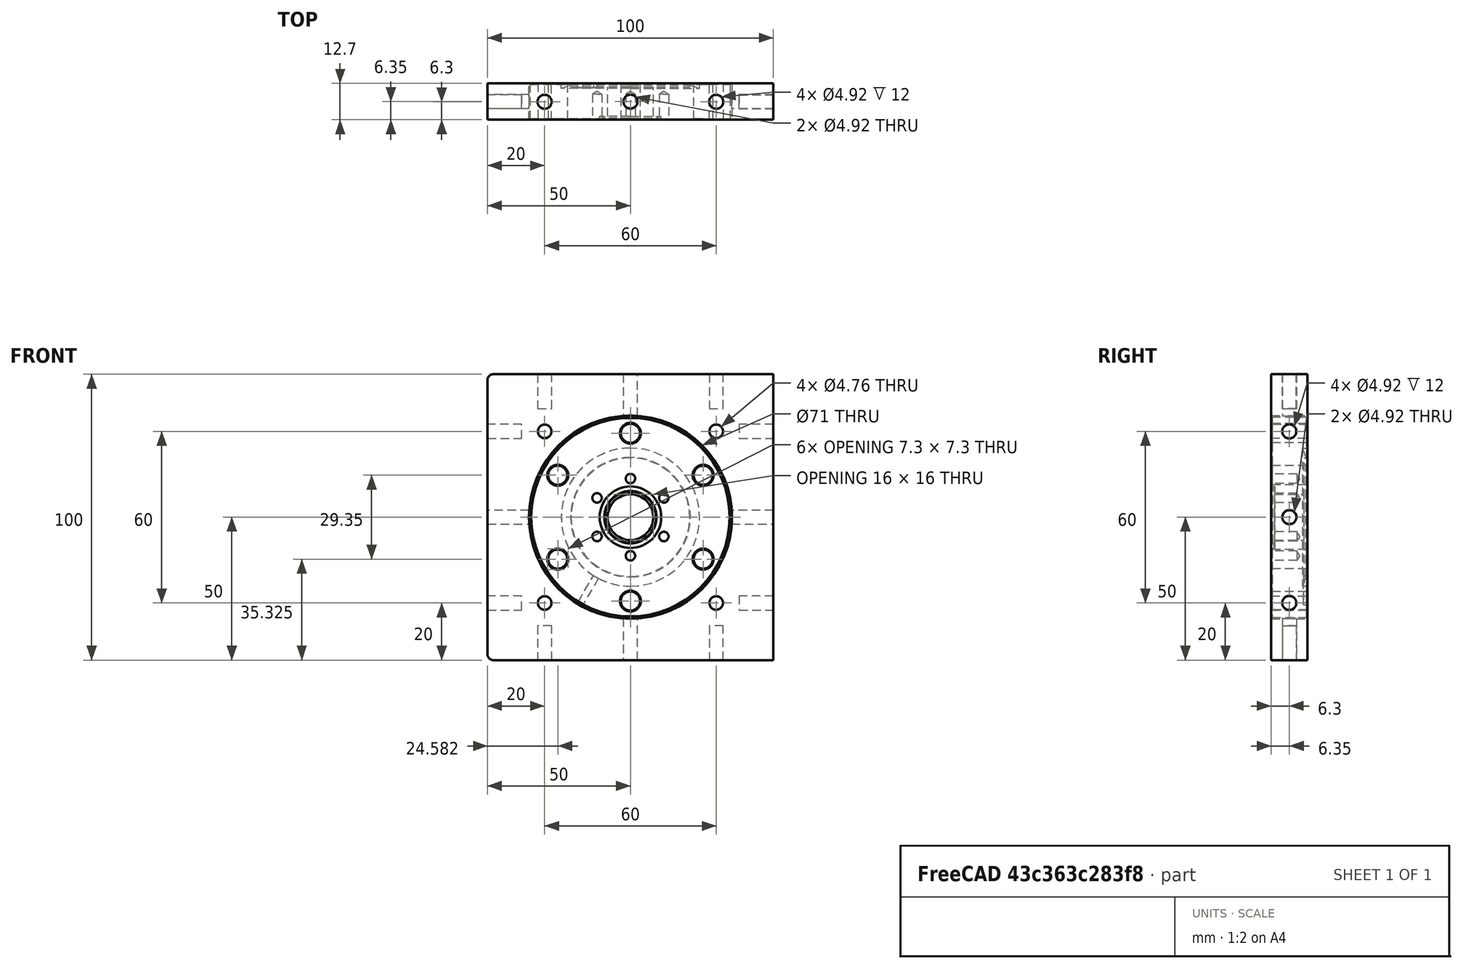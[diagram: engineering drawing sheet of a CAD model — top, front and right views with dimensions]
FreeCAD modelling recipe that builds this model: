
FCSTD DOCUMENT  (FreeCAD 0.20R29603 (Git))
Label: MechanicalCF35Mount001
License: All rights reserved
LicenseURL: http://en.wikipedia.org/wiki/All_rights_reserved
objects: Part::Feature×20, Part::Cylinder×15, TechDraw::DrawViewDimension×13, Part::Compound×12, TechDraw::DrawProjGroupItem×5, Part::Cut×4, Part::Box×1, Part::Fillet×1, TechDraw::DrawSVGTemplate×1, TechDraw::DrawProjGroup×1, TechDraw::DrawPage×1
note: 53 computed .brp shape members not serialized (recipe doc carries the construction recipe); baked Part::Feature solids carry a one-line shape summary decoded from their .brp

FEATURE [Part::Feature] Solid  label="Hositrad_CFA35-16D"
  shape: bbox 70 x 12.7 x 70 mm, 88 faces (baked)
FEATURE [Part::Feature] _7192_01_CF
  shape: bbox 33.78 x 40.23 x 14.22 mm, 39 faces, 0 solids (baked)
FEATURE [Part::Feature] _7192_01_CF001
  Placement = pos=(0,0,-39.0113) rot=(1,0,0;1.5708rad)
  shape: bbox 14 x 7.506 x 26.34 mm, 46 faces, 0 solids (baked)
FEATURE [Part::Feature] _7192_01_CF002
  Placement = pos=(0,0,-58.2625) rot=(-0.03621,0.706643,0.706643;3.21398rad)
  shape: bbox 18.12 x 10.39 x 7.838 mm, 29 faces, 0 solids (baked)
FEATURE [Part::Feature] _7192_01_CF003
  Placement = pos=(0,0,-42.2965) rot=(0.8891,-0.323652,-0.323652;1.68807rad)
  shape: bbox 16.99 x 16.03 x 5.603 mm, 25 faces, 0 solids (baked)
FEATURE [Part::Feature] _7192_01_CF004
  Placement = pos=(0,0,-35.56) rot=(0,0.707107,-0.707107;3.14159rad)
  shape: bbox 22.78 x 12.72 x 33.85 mm, 35 faces, 0 solids (baked)
FEATURE [Part::Feature] _7192_01_CF005
  Placement = pos=(0,0,-36.7339) rot=(0.997746,-0.047454,-0.047454;1.57305rad)
  shape: bbox 7.007 x 7.007 x 0.8128 mm, 6 faces, 0 solids (baked)
FEATURE [Part::Feature] _7192_01_CF006
  Placement = pos=(0,0,-66.0654) rot=(0.57735,0.57735,0.57735;2.0944rad)
  shape: bbox 2.416 x 2.416 x 39.37 mm, 29 faces, 0 solids (baked)
FEATURE [Part::Feature] _7192_01_CF007
  Placement = pos=(0,0,-32.2253) rot=(0.196732,0.693288,-0.693288;3.5301rad)
  shape: bbox 26.96 x 26.96 x 13.28 mm, 55 faces, 0 solids (baked)
FEATURE [Part::Feature] _7192_01_CF008
  Placement = pos=(0,0,-46.1699) rot=(0.196732,0.693288,-0.693288;3.5301rad)
  shape: bbox 34.28 x 29.27 x 4.775 mm, 16 faces, 0 solids (baked)
FEATURE [Part::Feature] _7192_01_CF009
  Placement = pos=(0,0,-22.86) rot=(0.196732,0.693288,-0.693288;3.5301rad)
  shape: bbox 24.3 x 24.3 x 12.6 mm, 19 faces, 0 solids (baked)
FEATURE [Part::Feature] _7192_01_CF010
  Placement = pos=(0,0,-12.7) rot=(0.196732,0.693288,-0.693288;3.5301rad)
  shape: bbox 26.42 x 26.42 x 12.7 mm, 14 faces, 0 solids (baked)
FEATURE [Part::Feature] _7192_01_CF011
  Placement = pos=(0,0,-42.1821) rot=(0.196732,0.693288,-0.693288;3.5301rad)
  shape: bbox 43.95 x 37.52 x 5.044 mm, 27 faces, 0 solids (baked)
FEATURE [Part::Feature] _7192_01_CF012
  Placement = pos=(0,0,-35.56) rot=(0.079728,0.704856,0.704856;2.98247rad)
  shape: bbox 15.4 x 15.4 x 39.12 mm, 6 faces, 0 solids (baked)
FEATURE [Part::Feature] _7192_01_CF013
  Placement = pos=(0,0,-26.6954) rot=(0.165786,0.697322,0.697322;2.81301rad)
  shape: bbox 5.339 x 4.281 x 34.06 mm, 6 faces, 0 solids (baked)
FEATURE [Part::Feature] _7192_01_CF014
  Placement = pos=(0,0,6.7564) rot=(0.205998,0.691941,-0.691941;3.54791rad)
  shape: bbox 9.907 x 7.446 x 1.311 mm, 4 faces, 0 solids (baked)
FEATURE [Part::Feature] _7192_01_CF015
  Placement = pos=(0,0,-7.9756) rot=(1,0,0;1.5708rad)
  shape: bbox 22.78 x 12.72 x 22.32 mm, 35 faces, 0 solids (baked)
FEATURE [Part::Feature] _7192_01_CF016
  Placement = pos=(0,0,22.3805) rot=(0.205998,0.691941,-0.691941;3.54791rad)
  shape: bbox 3.344 x 3.344 x 15.27 mm, 29 faces, 0 solids (baked)
FEATURE [Part::Feature] _7192_01_CF017
  Placement = pos=(0,0,6.7564) rot=(1,0,0;1.5708rad)
  shape: bbox 10.8 x 10.8 x 1.524 mm, 10 faces, 0 solids (baked)
FEATURE [Part::Compound] Compound  label="CF16BNCFeedthrough"
  Links = -> [_7192_01_CF,_7192_01_CF001,_7192_01_CF002,_7192_01_CF003,_7192_01_CF004,_7192_01_CF005,_7192_01_CF006,_7192_01_CF007,_7192_01_CF008,_7192_01_CF009,_7192_01_CF010,_7192_01_CF011,_7192_01_CF012,_7192_01_CF013,_7192_01_CF014,_7192_01_CF015,_7192_01_CF016,_7192_01_CF017]
  Placement = pos=(0,0,0) rot=(-1,0,0;1.5708rad)
FEATURE [Part::Box] Box  label="Würfel"
  AttacherType = Attacher::AttachEngine3D
  Height = 100
  Length = 100
  Placement = pos=(-50,0,-50) rot=(0,0,1;0rad)
  Width = 12.7
FEATURE [Part::Cylinder] Cylinder  label="Zylinder"
  Angle = 360
  AttacherType = Attacher::AttachEngine3D
  FirstAngle = 0
  Height = 12.7
  Placement = pos=(0,12.7,0) rot=(1,0,0;1.5708rad)
  Radius = 35.5
  SecondAngle = 0
FEATURE [Part::Cut] Cut
  Base = -> Box
  Tool = -> Cylinder
FEATURE [Part::Cylinder] Cylinder001  label="Zylinder001"
  Angle = 360
  AttacherType = Attacher::AttachEngine3D
  FirstAngle = 0
  Height = 100
  Placement = pos=(0,6.35,-50) rot=(0,0,1;0rad)
  Radius = 2.46
  SecondAngle = 0
FEATURE [Part::Cylinder] Cylinder002  label="Zylinder002"
  Angle = 360
  AttacherType = Attacher::AttachEngine3D
  FirstAngle = 0
  Height = 100
  Placement = pos=(0,6.35,-50) rot=(0,0,1;0rad)
  Radius = 2.46
  SecondAngle = 0
FEATURE [Part::Compound] Compound001
  Links = -> [Cylinder002]
  Placement = pos=(0,0,0) rot=(0,1,0;1.5708rad)
FEATURE [Part::Compound] Compound002  label="SetscrewCoreholes"
  Links = -> [Compound001,Cylinder001]
FEATURE [Part::Cut] Cut001
  Base = -> Cut
  Tool = -> Compound002
FEATURE [Part::Cylinder] Cylinder003  label="Zylinder003"
  Angle = 360
  AttacherType = Attacher::AttachEngine3D
  FirstAngle = 0
  Height = 12
  Placement = pos=(-30,6.3,-50) rot=(0,0,1;0rad)
  Radius = 2.46
  SecondAngle = 0
FEATURE [Part::Cylinder] Cylinder004  label="Zylinder004"
  Angle = 360
  AttacherType = Attacher::AttachEngine3D
  FirstAngle = 0
  Height = 12
  Placement = pos=(30,6.3,-50) rot=(0,0,1;0rad)
  Radius = 2.46
  SecondAngle = 0
FEATURE [Part::Compound] Compound003
  Links = -> [Cylinder003,Cylinder004]
FEATURE [Part::Cylinder] Cylinder005  label="Zylinder005"
  Angle = 360
  AttacherType = Attacher::AttachEngine3D
  FirstAngle = 0
  Height = 12
  Placement = pos=(-30,6.3,-50) rot=(0,0,1;0rad)
  Radius = 2.46
  SecondAngle = 0
FEATURE [Part::Cylinder] Cylinder006  label="Zylinder006"
  Angle = 360
  AttacherType = Attacher::AttachEngine3D
  FirstAngle = 0
  Height = 12
  Placement = pos=(30,6.3,-50) rot=(0,0,1;0rad)
  Radius = 2.46
  SecondAngle = 0
FEATURE [Part::Compound] Compound004
  Links = -> [Cylinder005,Cylinder006]
  Placement = pos=(0,0,0) rot=(0,-1,0;1.5708rad)
FEATURE [Part::Cylinder] Cylinder007  label="Zylinder007"
  Angle = 360
  AttacherType = Attacher::AttachEngine3D
  FirstAngle = 0
  Height = 12
  Placement = pos=(-30,6.3,-50) rot=(0,0,1;0rad)
  Radius = 2.46
  SecondAngle = 0
FEATURE [Part::Cylinder] Cylinder008  label="Zylinder008"
  Angle = 360
  AttacherType = Attacher::AttachEngine3D
  FirstAngle = 0
  Height = 12
  Placement = pos=(30,6.3,-50) rot=(0,0,1;0rad)
  Radius = 2.46
  SecondAngle = 0
FEATURE [Part::Compound] Compound005
  Links = -> [Cylinder007,Cylinder008]
  Placement = pos=(0,0,0) rot=(0,1,0;3.14159rad)
FEATURE [Part::Cylinder] Cylinder009  label="Zylinder009"
  Angle = 360
  AttacherType = Attacher::AttachEngine3D
  FirstAngle = 0
  Height = 12
  Placement = pos=(-30,6.3,-50) rot=(0,0,1;0rad)
  Radius = 2.46
  SecondAngle = 0
FEATURE [Part::Cylinder] Cylinder010  label="Zylinder010"
  Angle = 360
  AttacherType = Attacher::AttachEngine3D
  FirstAngle = 0
  Height = 12
  Placement = pos=(30,6.3,-50) rot=(0,0,1;0rad)
  Radius = 2.46
  SecondAngle = 0
FEATURE [Part::Compound] Compound006
  Links = -> [Cylinder009,Cylinder010]
  Placement = pos=(0,0,0) rot=(0,1,0;-4.71239rad)
FEATURE [Part::Compound] Compound007  label="M6Mountscrews"
  Links = -> [Compound003,Compound004,Compound005,Compound006]
FEATURE [Part::Cut] Cut002
  Base = -> Cut001
  Tool = -> Compound007
FEATURE [Part::Cylinder] Cylinder011  label="Zylinder011"
  Angle = 360
  AttacherType = Attacher::AttachEngine3D
  FirstAngle = 0
  Height = 300
  Placement = pos=(30,12.7,30) rot=(1,0,0;1.5708rad)
  Radius = 2.38
  SecondAngle = 0
FEATURE [Part::Cylinder] Cylinder012  label="Zylinder012"
  Angle = 360
  AttacherType = Attacher::AttachEngine3D
  FirstAngle = 0
  Height = 300
  Placement = pos=(30,12.7,30) rot=(1,0,0;1.5708rad)
  Radius = 2.38
  SecondAngle = 0
FEATURE [Part::Compound] Compound008
  Links = -> [Cylinder012]
  Placement = pos=(0,0,0) rot=(0,1,0;1.5708rad)
FEATURE [Part::Cylinder] Cylinder013  label="Zylinder013"
  Angle = 360
  AttacherType = Attacher::AttachEngine3D
  FirstAngle = 0
  Height = 300
  Placement = pos=(30,12.7,30) rot=(1,0,0;1.5708rad)
  Radius = 2.38
  SecondAngle = 0
FEATURE [Part::Compound] Compound009
  Links = -> [Cylinder013]
  Placement = pos=(0,0,0) rot=(0,1,0;3.14159rad)
FEATURE [Part::Cylinder] Cylinder014  label="Zylinder014"
  Angle = 360
  AttacherType = Attacher::AttachEngine3D
  FirstAngle = 0
  Height = 300
  Placement = pos=(30,12.7,30) rot=(1,0,0;1.5708rad)
  Radius = 2.38
  SecondAngle = 0
FEATURE [Part::Compound] Compound010
  Links = -> [Cylinder014]
  Placement = pos=(0,0,0) rot=(0,-1,0;1.5708rad)
FEATURE [Part::Compound] Compound014  label="M6ThreadRods"
  Links = -> [Cylinder011,Compound008,Compound009,Compound010]
FEATURE [Part::Cut] Cut003
  Base = -> Cut002
  Tool = -> Compound014
FEATURE [Part::Fillet] Fillet
  Base = -> Cut003
  Edges = 2 edges r=2: [Edge2,Edge3]
FEATURE [Part::Feature] Fillet_solid  label="Fillet (Solid)"
  shape: bbox 100 x 12.7 x 100 mm, 33 faces (baked)
FEATURE [TechDraw::DrawSVGTemplate] Template
  EditableTexts = Designed_by_Name=Thomas Spielauer; FC-Date=2023-07-05; FC-SC=mm; FC-SH=01; FC-Title=CF40 electronics housing; Subtitle=Front plate
  Height = 210
  Orientation = 1
  Width = 297
FEATURE [TechDraw::DrawProjGroupItem] ProjItem  label="Front"
  CoarseView = false
  Direction = (0,-1,0)
  Focus = 100
  HardHidden = false
  IsoCount = 0
  IsoHidden = false
  IsoVisible = false
  LockPosition = true
  Perspective = false
  Rotation = 0
  RotationVector = (0,0,1)
  ScaleType = 2
  SeamHidden = false
  SeamVisible = true
  SmoothHidden = false
  SmoothVisible = true
  Source = -> [Fillet]
  Type = 0
  X = 0
  XDirection = (0,0,1)
  Y = 0
FEATURE [TechDraw::DrawProjGroupItem] ProjItem001  label="Right"
  CoarseView = false
  Direction = (0,-1e-16,1)
  Focus = 100
  HardHidden = false
  IsoCount = 0
  IsoHidden = false
  IsoVisible = false
  LockPosition = false
  Perspective = false
  Rotation = 0
  RotationVector = (1,0,0)
  ScaleType = 2
  SeamHidden = false
  SeamVisible = true
  SmoothHidden = false
  SmoothVisible = true
  Source = -> [Fillet]
  Type = 2
  X = -67.6611
  XDirection = (0,1,1e-16)
  Y = 0
FEATURE [TechDraw::DrawProjGroupItem] ProjItem002  label="Bottom"
  CoarseView = false
  Direction = (1,0,0)
  Focus = 100
  HardHidden = false
  IsoCount = 0
  IsoHidden = false
  IsoVisible = false
  LockPosition = false
  Perspective = false
  Rotation = 0
  RotationVector = (1,0,0)
  ScaleType = 2
  SeamHidden = false
  SeamVisible = true
  SmoothHidden = false
  SmoothVisible = true
  Source = -> [Fillet]
  Type = 5
  X = 0
  XDirection = (0,0,1)
  Y = 73.816
FEATURE [TechDraw::DrawProjGroupItem] ProjItem003  label="Left"
  CoarseView = false
  Direction = (0,-1e-16,-1)
  Focus = 100
  HardHidden = false
  IsoCount = 0
  IsoHidden = false
  IsoVisible = false
  LockPosition = false
  Perspective = false
  Rotation = 0
  RotationVector = (1,0,0)
  ScaleType = 2
  SeamHidden = false
  SeamVisible = true
  SmoothHidden = false
  SmoothVisible = true
  Source = -> [Fillet]
  Type = 1
  X = 105.155
  XDirection = (0,-1,1e-16)
  Y = 0
FEATURE [TechDraw::DrawProjGroupItem] ProjItem004  label="Top"
  CoarseView = false
  Direction = (-1,0,0)
  Focus = 100
  HardHidden = false
  IsoCount = 0
  IsoHidden = false
  IsoVisible = false
  LockPosition = false
  Perspective = false
  Rotation = 0
  RotationVector = (1,0,0)
  ScaleType = 2
  SeamHidden = false
  SeamVisible = true
  SmoothHidden = false
  SmoothVisible = true
  Source = -> [Fillet]
  Type = 4
  X = 0
  XDirection = (0,0,1)
  Y = -75.3562
FEATURE [TechDraw::DrawProjGroup] ProjGroup
  Anchor = -> ProjItem
  AutoDistribute = true
  LockPosition = false
  ProjectionType = 0
  Rotation = 0
  ScaleType = 0
  Source = -> [Fillet]
  Views = -> [ProjItem,ProjItem001,ProjItem002,ProjItem003,ProjItem004]
  X = 91.0868
  Y = 118.279
  spacingX = 0
  spacingY = 0
FEATURE [TechDraw::DrawViewDimension] Dimension
  AngleOverride = false
  Arbitrary = false
  ArbitraryTolerances = false
  EqualTolerance = true
  ExtensionAngle = 0
  FormatSpec = %.2w
  FormatSpecOverTolerance = %+.2w
  FormatSpecUnderTolerance = %+.2w
  Inverted = false
  LineAngle = 0
  LockPosition = false
  MeasureType = 1
  OverTolerance = 0
  References2D = -> [ProjItem003]
  Rotation = 0
  ScaleType = 0
  TheoreticalExact = false
  Type = 0
  UnderTolerance = 0
  X = 27.7422
  Y = 2.49993
FEATURE [TechDraw::DrawViewDimension] Dimension001
  AngleOverride = false
  Arbitrary = false
  ArbitraryTolerances = false
  EqualTolerance = true
  ExtensionAngle = 0
  FormatSpec = %.2w
  FormatSpecOverTolerance = %+.2w
  FormatSpecUnderTolerance = %+.2w
  Inverted = false
  LineAngle = 0
  LockPosition = false
  MeasureType = 1
  OverTolerance = 0
  References2D = -> [ProjItem004]
  Rotation = 0
  ScaleType = 0
  TheoreticalExact = false
  Type = 0
  UnderTolerance = 0
  X = -0.515822
  Y = -20.0124
FEATURE [TechDraw::DrawViewDimension] Dimension002
  AngleOverride = false
  Arbitrary = false
  ArbitraryTolerances = false
  EqualTolerance = true
  ExtensionAngle = 0
  FormatSpec = ⌀%.2w
  FormatSpecOverTolerance = %+.2w
  FormatSpecUnderTolerance = %+.2w
  Inverted = false
  LineAngle = 0
  LockPosition = false
  MeasureType = 1
  OverTolerance = 0
  References2D = -> [ProjItem]
  Rotation = 0
  ScaleType = 0
  TheoreticalExact = false
  Type = 5
  UnderTolerance = 0
  X = 0.325472
  Y = 8.03302
FEATURE [TechDraw::DrawViewDimension] Dimension003
  AngleOverride = false
  Arbitrary = false
  ArbitraryTolerances = false
  EqualTolerance = true
  ExtensionAngle = 0
  FormatSpec = ⌀%.2w (M6 4x)
  FormatSpecOverTolerance = %+.2w
  FormatSpecUnderTolerance = %+.2w
  Inverted = false
  LineAngle = 0
  LockPosition = false
  MeasureType = 1
  OverTolerance = 0
  References2D = -> [ProjItem]
  Rotation = 0
  ScaleType = 0
  TheoreticalExact = false
  Type = 5
  UnderTolerance = 0
  X = -23.9583
  Y = 40.0197
FEATURE [TechDraw::DrawViewDimension] Dimension004
  AngleOverride = false
  Arbitrary = false
  ArbitraryTolerances = false
  EqualTolerance = true
  ExtensionAngle = 0
  FormatSpec = %.2w
  FormatSpecOverTolerance = %+.2w
  FormatSpecUnderTolerance = %+.2w
  Inverted = false
  LineAngle = 0
  LockPosition = false
  MeasureType = 1
  OverTolerance = 0
  References2D = -> [ProjItem]
  Rotation = 0
  ScaleType = 0
  TheoreticalExact = false
  Type = 0
  UnderTolerance = 0
  X = 39.4213
  Y = 67.0173
FEATURE [TechDraw::DrawViewDimension] Dimension005
  AngleOverride = false
  Arbitrary = false
  ArbitraryTolerances = false
  EqualTolerance = true
  ExtensionAngle = 0
  FormatSpec = %.2w
  FormatSpecOverTolerance = %+.2w
  FormatSpecUnderTolerance = %+.2w
  Inverted = false
  LineAngle = 0
  LockPosition = false
  MeasureType = 1
  OverTolerance = 0
  References2D = -> [ProjItem]
  Rotation = 0
  ScaleType = 0
  TheoreticalExact = false
  Type = 0
  UnderTolerance = 0
  X = 34.38
  Y = 42.4999
FEATURE [TechDraw::DrawViewDimension] Dimension006
  AngleOverride = false
  Arbitrary = false
  ArbitraryTolerances = false
  EqualTolerance = true
  ExtensionAngle = 0
  FormatSpec = %.2w
  FormatSpecOverTolerance = %+.2w
  FormatSpecUnderTolerance = %+.2w
  Inverted = false
  LineAngle = 0
  LockPosition = false
  MeasureType = 1
  OverTolerance = 0
  References2D = -> [ProjItem]
  Rotation = 0
  ScaleType = 0
  TheoreticalExact = false
  Type = 0
  UnderTolerance = 0
  X = 71.4033
  Y = -19.5166
FEATURE [TechDraw::DrawViewDimension] Dimension007
  AngleOverride = false
  Arbitrary = false
  ArbitraryTolerances = false
  EqualTolerance = true
  ExtensionAngle = 0
  FormatSpec = %.2w
  FormatSpecOverTolerance = %+.2w
  FormatSpecUnderTolerance = %+.2w
  Inverted = false
  LineAngle = 0
  LockPosition = false
  MeasureType = 1
  OverTolerance = 0
  References2D = -> [ProjItem]
  Rotation = 0
  ScaleType = 0
  TheoreticalExact = false
  Type = 0
  UnderTolerance = 0
  X = -1.26969
  Y = 60.8859
FEATURE [TechDraw::DrawViewDimension] Dimension008
  AngleOverride = false
  Arbitrary = false
  ArbitraryTolerances = false
  EqualTolerance = true
  ExtensionAngle = 0
  FormatSpec = ⌀%.2w (M6 3x pro Seite)
  FormatSpecOverTolerance = %+.2w
  FormatSpecUnderTolerance = %+.2w
  Inverted = false
  LineAngle = 0
  LockPosition = false
  MeasureType = 1
  OverTolerance = 0
  References2D = -> [ProjItem003]
  Rotation = 0
  ScaleType = 0
  TheoreticalExact = false
  Type = 5
  UnderTolerance = 0
  X = 55.193
  Y = 36.5443
FEATURE [TechDraw::DrawViewDimension] Dimension009
  AngleOverride = false
  Arbitrary = false
  ArbitraryTolerances = false
  EqualTolerance = true
  ExtensionAngle = 0
  FormatSpec = %.2w
  FormatSpecOverTolerance = %+.2w
  FormatSpecUnderTolerance = %+.2w
  Inverted = false
  LineAngle = 0
  LockPosition = false
  MeasureType = 1
  OverTolerance = 0
  References2D = -> [ProjItem003]
  Rotation = 0
  ScaleType = 0
  TheoreticalExact = false
  Type = 0
  UnderTolerance = 0
  X = -14.0854
  Y = 64.8143
FEATURE [TechDraw::DrawViewDimension] Dimension010
  AngleOverride = false
  Arbitrary = false
  ArbitraryTolerances = false
  EqualTolerance = true
  ExtensionAngle = 0
  FormatSpec = %.2w
  FormatSpecOverTolerance = %+.2w
  FormatSpecUnderTolerance = %+.2w
  Inverted = false
  LineAngle = 0
  LockPosition = false
  MeasureType = 1
  OverTolerance = 0
  References2D = -> [ProjItem003]
  Rotation = 0
  ScaleType = 0
  TheoreticalExact = false
  Type = 0
  UnderTolerance = 0
  X = -20.8153
  Y = 17.1561
FEATURE [TechDraw::DrawViewDimension] Dimension011
  AngleOverride = false
  Arbitrary = false
  ArbitraryTolerances = false
  EqualTolerance = true
  ExtensionAngle = 0
  FormatSpec = %.2w
  FormatSpecOverTolerance = %+.2w
  FormatSpecUnderTolerance = %+.2w
  Inverted = false
  LineAngle = 0
  LockPosition = false
  MeasureType = 1
  OverTolerance = 0
  References2D = -> [ProjItem003]
  Rotation = 0
  ScaleType = 0
  TheoreticalExact = false
  Type = 0
  UnderTolerance = 0
  X = -20.7966
  Y = -12.5001
FEATURE [TechDraw::DrawViewDimension] Dimension012
  AngleOverride = false
  Arbitrary = false
  ArbitraryTolerances = false
  EqualTolerance = true
  ExtensionAngle = 0
  FormatSpec = %.2w
  FormatSpecOverTolerance = %+.2w
  FormatSpecUnderTolerance = %+.2w
  Inverted = false
  LineAngle = 0
  LockPosition = false
  MeasureType = 1
  OverTolerance = 0
  References2D = -> [ProjItem003]
  Rotation = 0
  ScaleType = 0
  TheoreticalExact = false
  Type = 0
  UnderTolerance = 0
  X = 15.28
  Y = -53.2031
FEATURE [TechDraw::DrawPage] Page
  KeepUpdated = true
  NextBalloonIndex = 1
  ProjectionType = 0
  Template = -> Template
  Views = -> [ProjGroup,Dimension,Dimension001,Dimension002,Dimension003,Dimension004,Dimension005,Dimension006,Dimension007,Dimension008,Dimension009,Dimension010,Dimension011,Dimension012]
